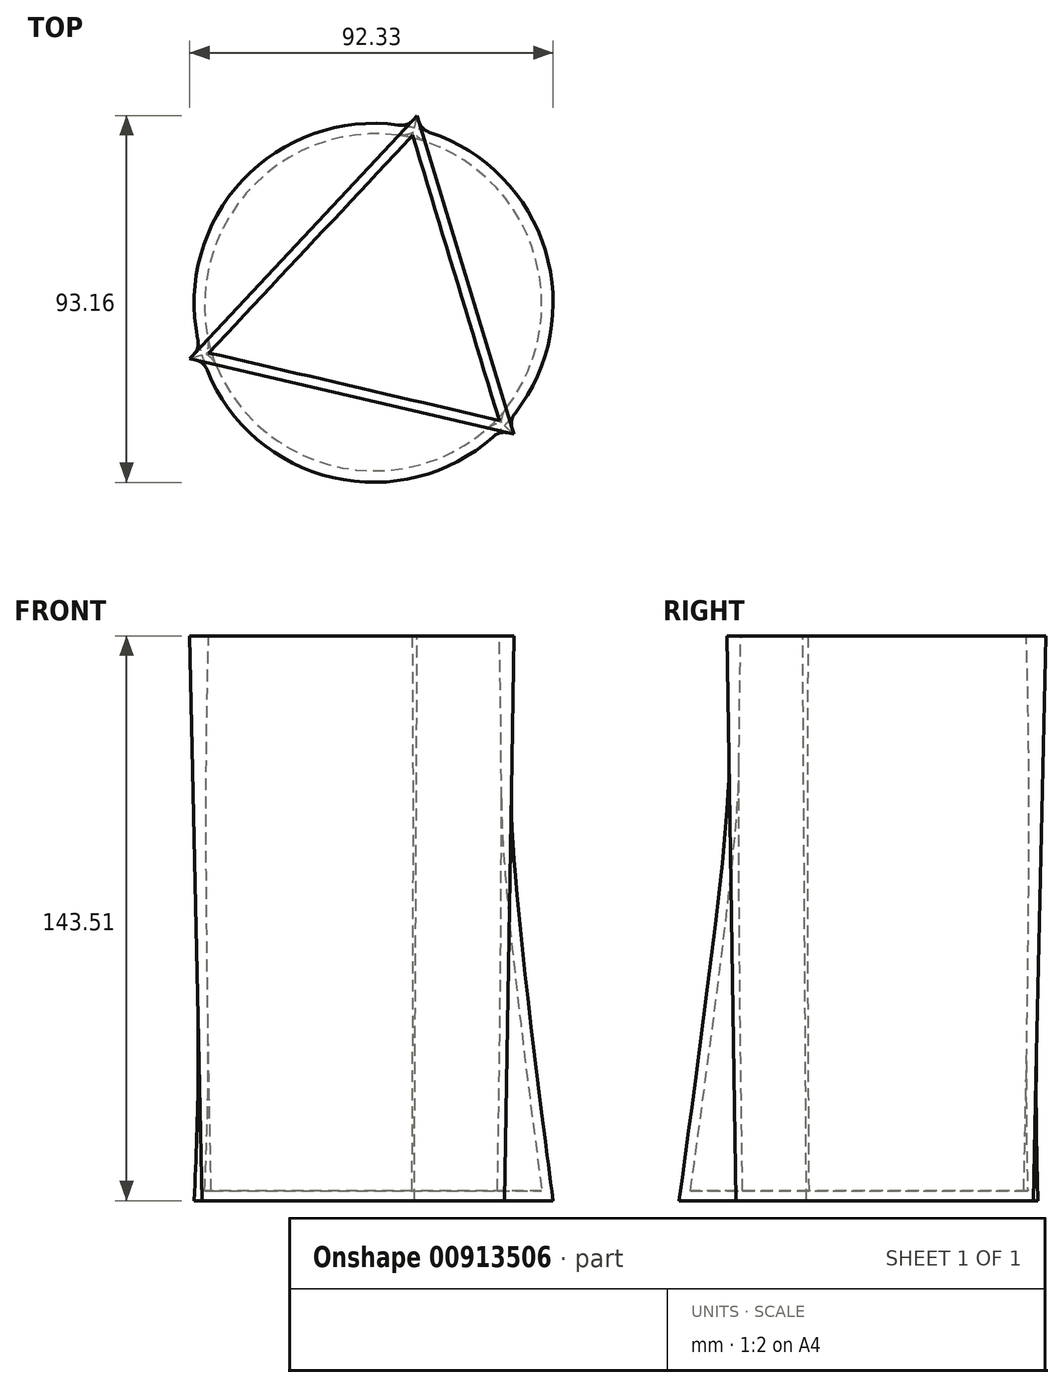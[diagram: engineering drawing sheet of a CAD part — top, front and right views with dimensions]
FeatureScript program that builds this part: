
annotation { "Feature Type Name" : "Feature", "Feature Type Description" : "" }
export const myFeature = defineFeature(function(context is Context, id is Id, definition is map)
    precondition{}
    {
        {
            var Q0;
            Q0=qCreatedBy(makeId("Top.planeOp"),FACE);
            var sketch = newSketch(context, id + "F0", { "sketchPlane" : qUnion([Q0])});
            skCircle(sketch, "E0", {"center": v(0, 0) * mm, "radius": 45.6 * mm});
            skSolve(sketch);
        }
        {
            var Q0;
            Q0=makeQuery(id+"F0.imprint","IMPRINT",FACE,{"disambiguationData":[TD([[makeQuery(id+"F0.imprint","IMPRINT",EDGE,{"derivedFrom":sQuery(id+"F0.wireOp",EDGE,"E0")}),1.0]])]});
            cPlane(context, id + "F1", {"entities" : qUnion([Q0]), "cplaneType" : CPlaneType.OFFSET, "offset" : 143.5 * mm, "width" : 152.4 * mm, "height" : 152.4 * mm});
        }
        {
            var Q0;
            Q0=qCreatedBy(id+"F1.planeOp",FACE);
            var sketch = newSketch(context, id + "F2", { "sketchPlane" : qUnion([Q0])});
            skCircle(sketch, "E1.cCircle", {"center": v(0, 0) * mm, "radius": 24.42 * mm, "construction": true});
            skLineSegment(sketch, "E1.0", {"start": v(-46.73, -14.18) * mm, "end": v(11.08, 47.56) * mm});
            skLineSegment(sketch, "E1.1", {"start": v(11.08, 47.56) * mm, "end": v(35.65, -33.38) * mm});
            skLineSegment(sketch, "E1.2", {"start": v(35.65, -33.38) * mm, "end": v(-46.73, -14.18) * mm});
            skPoint(sketch, "E1.0.midPoint", {"position": v(-17.82, 16.69) * mm});
            skSolve(sketch);
        }
        {
            var Q0;
            Q0=makeQuery(id+"F0.imprint","IMPRINT",FACE,{"disambiguationData":[TD([[makeQuery(id+"F0.imprint","IMPRINT",EDGE,{"derivedFrom":sQuery(id+"F0.wireOp",EDGE,"E0")}),1.0]])]});
            var Q1;
            Q1=makeQuery(id+"F2.imprint","IMPRINT",FACE,{"disambiguationData":[TD([[makeQuery(id+"F2.imprint","IMPRINT",EDGE,{"derivedFrom":sQuery(id+"F2.wireOp",EDGE,"E1.0")}),-1.0]])]});
            loft(context, id + "F3", {"sheetProfilesArray" : [{ "sheetProfileEntities" : qUnion([Q0]) }, { "sheetProfileEntities" : qUnion([Q1]) }]});
        }
        {
            var Q0;
            Q0=makeQuery(id+"F3.opLoft","CAP_FACE",FACE,{"disambiguationData":[OSD([makeQuery(id+"F2.imprint","IMPRINT",FACE,{"disambiguationData":[TD([[makeQuery(id+"F2.imprint","IMPRINT",EDGE,{"derivedFrom":sQuery(id+"F2.wireOp",EDGE,"E1.0")}),-1.0]])]})])],"isStart":true});
            shell(context, id + "F4", {"entities" : qUnion([Q0]), "thickness" : 2.54 * mm});
        }
    });
